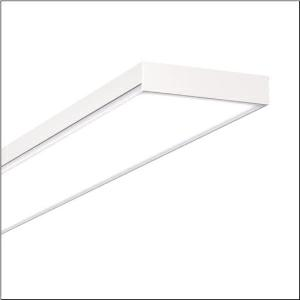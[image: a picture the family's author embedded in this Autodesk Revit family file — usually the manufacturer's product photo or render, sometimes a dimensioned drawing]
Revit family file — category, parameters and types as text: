
# Revit family: apollon_r__31_surface_51mp26wm2441w_6455
name_source: partatom
category: Lighting Fixtures
units: mm (PartAtom-declared; Revit-internal decimal feet)

## family parameters
Cut with Voids When Loaded = No
Host = Face
Light Source = No
Part Type = Normal
Room Calculation Point = No
Round Connector Dimension = Use Diameter
Shared = No

## types (1)
- Apollon® 31 Surface (1 x LED, 4600 lm, 33 W, 4000K)
    Apparent Load = 33 VA
    CIE Flux Codes = 61 87 97 97 100
    Color Rendering = 80
    Color Temperature = 4000K
    Default Elevation = 1800 mm
    Description = Apollon® 31 Surface, office luminaire, primary optical cover: micro prismatic cover, of PMMA, light emission: direct distribution, primary light characteristic: symmetric, installation type: surface-mounted, LED, rated luminous flux: 4.600lm, luminous efficacy: 139lm/W, light colour: 840, colour temperature: 4000K, control gear: ECG Multilumen, with terminal, 3-pole, mains connection: 220..240V, AC, 50/60Hz, rated input power: 33W, housing, of sheet steel, coil coated, traffic white (RAL 9016), length: 1.545mm, width: 200mm, height: 44mm, protection rating (complete): IP20, insulation class (complete): insulation class II (safety insulation), certification: CE, impact resistance: IK02, permissible operating ambient temperature: -20..+40°C, packaging unit: 1 piece
    Height = 44 mm
    Lamp = 1 x LED
    Lamp Light Flux = 4600 lm
    Lamp Power = 33 W
    Lamp count = 1
    Length = 1545 mm
    Luminous efficacy = 139 lm/W
    Manufacturer = Siteco
    ModVariant = No
    Model = 51MP26WM2441W
    Mounting Place = Ceiling
    Mounting Type = Surface mounted
    Number of Poles = 1
    OnlyDefault = Yes
    Power Factor = 1
    Product Name = Apollon® 31 Surface
    Product group = office luminaire | ceiling mounted
    ProductGroupID = 304
    Protection Class = Protection class II
    Protection Degree = IP 20
    RLX_Detail_Level = 1
    RLX_Emergency_Light_Flux = 0 lm
    RLX_Emergency_Type = 0
    RLX_Emergency_Type_DB = No
    RlxData = <blob elided: 20745 chars, md5=759062e7>
    Socket = socket
    Standby Power = 0 W
    System Light Flux = 4600 lm
    System Power = 33 W
    Type Comments = Product without accessories
    Type Image = l_1007095.jpg
    URL = http://relux.com
    VarID = ---
    Voltage = 0 V
    Weight = 0.00 kg
    Width = 200 mm  [stored 0.656168 ft]

note: [stored X ft] marks values corroborated as IEEE doubles in the binary element streams (Revit-internal decimal feet)

## geometry (parser evidence)
native form markers: Blend x4, Sweep x12
no freeform markers — native parametric forms only
